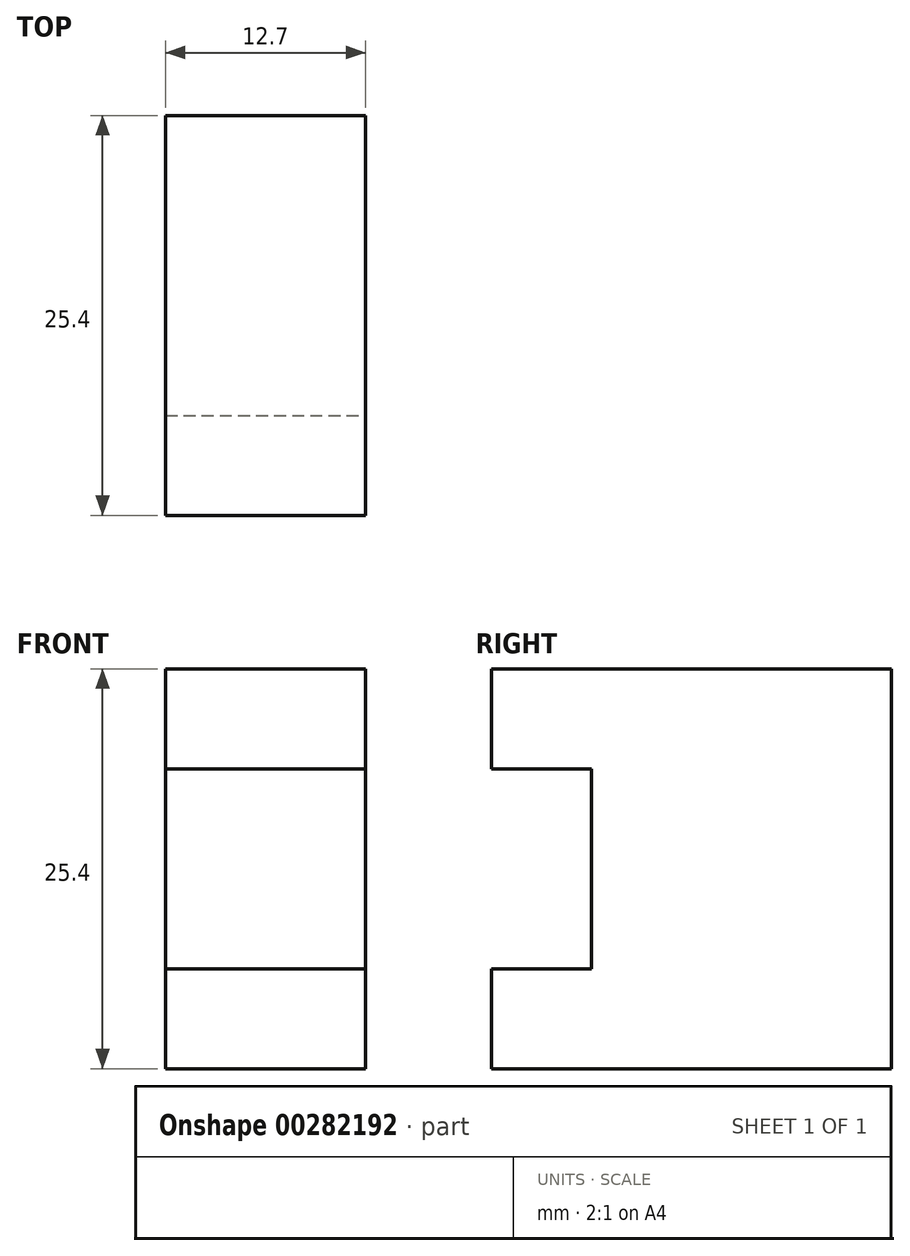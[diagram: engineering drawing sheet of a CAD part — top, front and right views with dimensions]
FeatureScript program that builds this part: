
annotation { "Feature Type Name" : "Feature", "Feature Type Description" : "" }
export const myFeature = defineFeature(function(context is Context, id is Id, definition is map)
    precondition{}
    {
        {
            var Q0;
            Q0=qCreatedBy(makeId("Front.planeOp"),FACE);
            var sketch = newSketch(context, id + "F0", { "sketchPlane" : qUnion([Q0])});
            skLineSegment(sketch, "E0.bottom", {"start": v(0, 12.7) * mm, "end": v(25.4, 12.7) * mm});
            skLineSegment(sketch, "E0.top", {"start": v(0, -12.7) * mm, "end": v(25.4, -12.7) * mm});
            skLineSegment(sketch, "E0.left", {"start": v(0, 12.7) * mm, "end": v(0, -12.7) * mm});
            skArc(sketch, "E1", {"start": v(25.4, -12.7) * mm, "mid": v(38.1, 0) * mm, "end": v(25.4, 12.7) * mm});
            skLineSegment(sketch, "E2", {"start": v(0, 12.7) * mm, "end": v(12.7, 12.7) * mm});
            skLineSegment(sketch, "E3", {"start": v(12.7, 12.7) * mm, "end": v(12.7, -12.7) * mm});
            skLineSegment(sketch, "E4", {"start": v(12.7, -12.7) * mm, "end": v(0, -12.7) * mm});
            skCircle(sketch, "E5", {"center": v(25.4, 0) * mm, "radius": 6.35 * mm});
            skSolve(sketch);
        }
        {
            var Q0;
            Q0=makeQuery(id+"F0.imprint","IMPRINT",FACE,{"disambiguationData":[TD([[makeQuery(id+"F0.imprint","IMPRINT",EDGE,{"derivedFrom":sQuery(id+"F0.wireOp",EDGE,"E0.left")}),1.0]])]});
            extrude(context, id + "F1", {"entities" : qUnion([Q0]), "depth" : 12.7 * mm});
        }
        {
            var Q0;
            Q0=makeQuery(id+"F0.imprint","IMPRINT",FACE,{"disambiguationData":[TD([[makeQuery(id+"F0.imprint","IMPRINT",EDGE,{"derivedFrom":sQuery(id+"F0.wireOp",EDGE,"E0.left")}),1.0]])]});
            extrude(context, id + "F2", {"entities" : qUnion([Q0]), "operationType" : NewBodyOperationType.ADD, "oppositeDirection" : true, "depth" : 12.7 * mm});
        }
        {
            var Q0;
            Q0=makeQuery(id+"F0.imprint","IMPRINT",FACE,{"disambiguationData":[TD([[makeQuery(id+"F0.imprint","IMPRINT",EDGE,{"derivedFrom":sQuery(id+"F0.wireOp",EDGE,"E0.bottom")}),-1.0]])]});
            extrude(context, id + "F3", {"entities" : qUnion([Q0]), "operationType" : NewBodyOperationType.ADD, "oppositeDirection" : true, "depth" : 12.7 * mm});
        }
        {
            var Q0;
            {var subQ0=sQuery(id+"F0.wireOp",EDGE,"E3");Q0=makeQuery(id+"F2.boolean.opBoolean","MERGE",FACE,{"derivedFrom":[makeQuery(id+"F1.opExtrude","SWEPT_FACE",FACE,{"disambiguationData":[OSD([subQ0])]}),makeQuery(id+"F2.opExtrude","SWEPT_FACE",FACE,{"disambiguationData":[OSD([subQ0])]})]});}
            var sketch = newSketch(context, id + "F4", { "sketchPlane" : qUnion([Q0])});
            skLineSegment(sketch, "E6.bottom", {"start": v(-12.7, 6.35) * mm, "end": v(-6.35, 6.35) * mm});
            skLineSegment(sketch, "E6.top", {"start": v(-12.7, -6.35) * mm, "end": v(-6.35, -6.35) * mm});
            skLineSegment(sketch, "E6.left", {"start": v(-12.7, 6.35) * mm, "end": v(-12.7, -6.35) * mm});
            skLineSegment(sketch, "E6.right", {"start": v(-6.35, 6.35) * mm, "end": v(-6.35, -6.35) * mm});
            skSolve(sketch);
        }
        {
            var Q0;
            Q0=makeQuery(id+"F4.imprint","IMPRINT",FACE,{"disambiguationData":[TD([[makeQuery(id+"F4.imprint","IMPRINT",EDGE,{"derivedFrom":sQuery(id+"F4.wireOp",EDGE,"E6.bottom")}),-1.0]])]});
            extrude(context, id + "F5", {"entities" : qUnion([Q0]), "operationType" : NewBodyOperationType.REMOVE, "oppositeDirection" : true, "depth" : 25.4 * mm});
        }
    });
